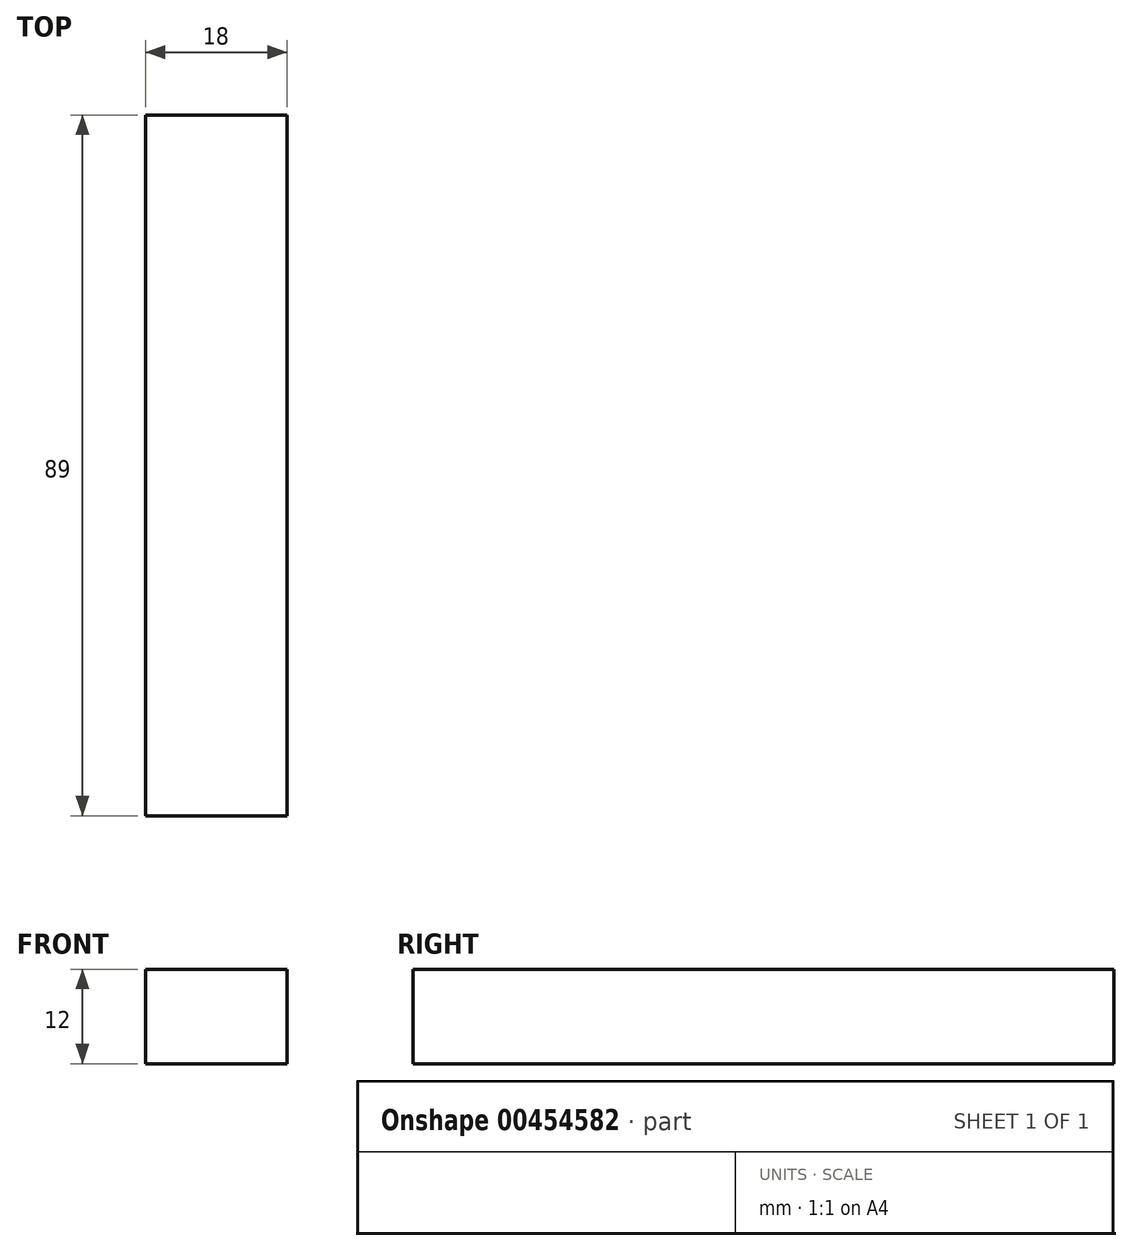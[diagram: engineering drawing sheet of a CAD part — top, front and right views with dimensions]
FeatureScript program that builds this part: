
annotation { "Feature Type Name" : "Feature", "Feature Type Description" : "" }
export const myFeature = defineFeature(function(context is Context, id is Id, definition is map)
    precondition{}
    {
        {
            var Q0;
            Q0=qCreatedBy(makeId("Front.planeOp"),FACE);
            var sketch = newSketch(context, id + "F0", { "sketchPlane" : qUnion([Q0])});
            skLineSegment(sketch, "E0.bottom", {"start": v(9, 6) * mm, "end": v(-9, 6) * mm});
            skLineSegment(sketch, "E0.top", {"start": v(9, -6) * mm, "end": v(-9, -6) * mm});
            skLineSegment(sketch, "E0.left", {"start": v(9, 6) * mm, "end": v(9, -6) * mm});
            skLineSegment(sketch, "E0.right", {"start": v(-9, 6) * mm, "end": v(-9, -6) * mm});
            skPoint(sketch, "E0.middle", {"position": v(0, 0) * mm});
            skSolve(sketch);
        }
        {
            var Q0;
            Q0 = qSketchRegion(id + "F0", true);
            extrude(context, id + "F1", {"entities" : qUnion([Q0]), "endBound" : BoundingType.SYMMETRIC, "depth" : 89 * mm});
        }
    });
